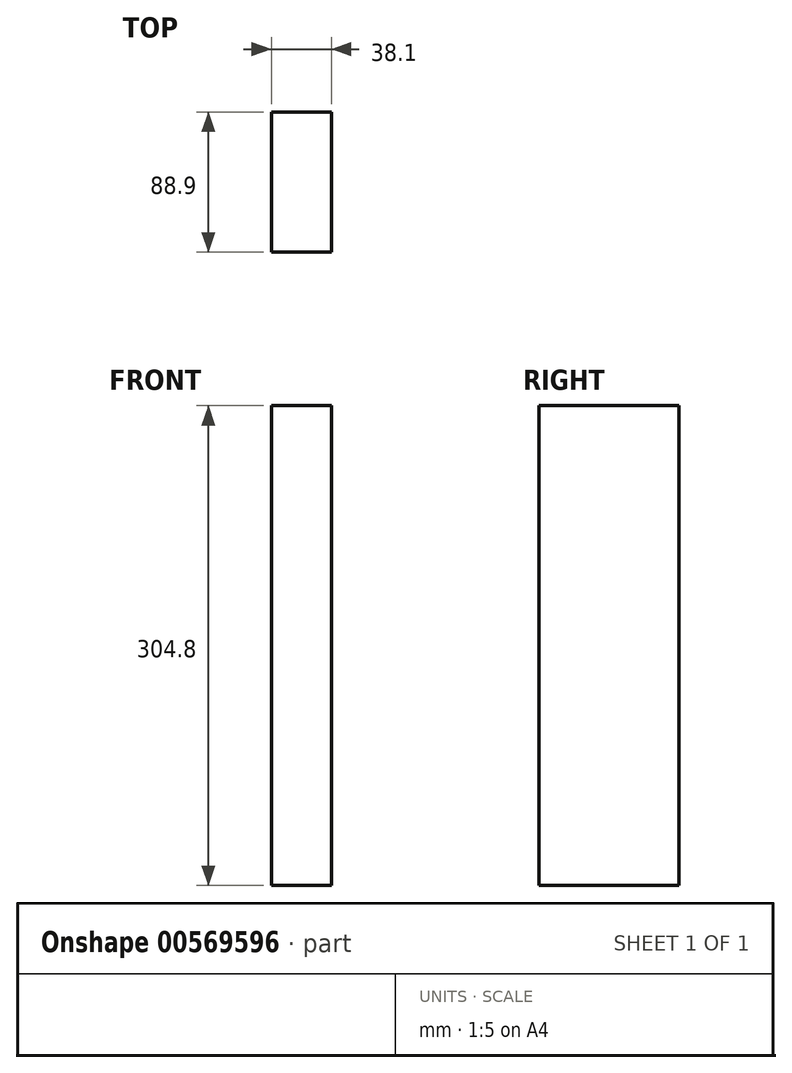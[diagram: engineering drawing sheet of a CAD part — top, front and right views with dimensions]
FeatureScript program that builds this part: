
annotation { "Feature Type Name" : "Feature", "Feature Type Description" : "" }
export const myFeature = defineFeature(function(context is Context, id is Id, definition is map)
    precondition{}
    {
        {
            var Q0;
            Q0=qCreatedBy(makeId("Front.planeOp"),FACE);
            var sketch = newSketch(context, id + "F0", { "sketchPlane" : qUnion([Q0])});
            skLineSegment(sketch, "E0.bottom", {"start": v(19.05, -152.4) * mm, "end": v(-19.05, -152.4) * mm});
            skLineSegment(sketch, "E0.top", {"start": v(19.05, 152.4) * mm, "end": v(-19.05, 152.4) * mm});
            skLineSegment(sketch, "E0.left", {"start": v(19.05, -152.4) * mm, "end": v(19.05, 152.4) * mm});
            skLineSegment(sketch, "E0.right", {"start": v(-19.05, -152.4) * mm, "end": v(-19.05, 152.4) * mm});
            skPoint(sketch, "E0.middle", {"position": v(0, 0) * mm});
            skSolve(sketch);
        }
        {
            var Q0;
            Q0 = qSketchRegion(id + "F0", true);
            extrude(context, id + "F1", {"entities" : qUnion([Q0]), "depth" : 88.9 * mm, "offsetDistance" : 25.4 * mm});
        }
    });
